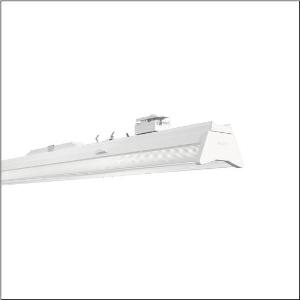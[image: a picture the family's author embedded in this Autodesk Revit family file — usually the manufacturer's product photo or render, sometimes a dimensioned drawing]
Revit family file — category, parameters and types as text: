
# Revit family: licross_r__21_performance_mo_52td16dn46xg_ca4f
name_source: partatom
category: Lighting Fixtures
units: mm (PartAtom-declared; Revit-internal decimal feet)

## family parameters
Cut with Voids When Loaded = No
Host = Face
Light Source = No
Part Type = Normal
Room Calculation Point = No
Round Connector Dimension = Use Diameter
Shared = No

## types (1)
- --- (1 x LED, 6000 lm, 32.7 W, 4000K)
    Apparent Load = 33 VA
    CIE Flux Codes = 66 88 96 79 100
    Color Rendering = 80
    Color Temperature = 4000K
    Default Elevation = 1800 mm
    Description = Licross® 21 Performance MO, luminaire insert, of sheet steel, galvanised, coil coated, white, length: 1.500mm, width: 120mm, height: 123mm, LED rated luminous flux: 6.000lm, light colour: 840, control gear: DALI 2, with plug, 5-pole, with phase selection, mains connection: 220..240V, AC, 50/60Hz, rated input power: 33W, halogen-free wiring, primary light control with lens, of plastic, primary optical cover: cover, of PMMA, light emission: direct/indirect distribution, primary light characteristic: symmetric, protection rating (complete): IP54, insulation class (complete): insulation class I (protective earthing), certification: CE, ENEC, VDE, UKCA, protection symbol: D if used in an environment with non-conductive dust loads with corresponding accessories, impact resistance: IK06, permissible ambient temperature for indoor applications: -25..+45°C, corresponds to IFS (International Featured Standards) requirements for safety and quality in the food industry, reducing of maximum allowable ambient temperature of 5°C with ceiling mounting, LABS conformity tested according to VDMA 24364:2018-05, packaging unit: 1 piece
    Height = 114 mm
    Lamp = 1 x LED
    Lamp Light Flux = 6000 lm
    Lamp Power = 32.7 W
    Lamp count = 1
    Length = 1500 mm
    Luminous efficacy = 183 lm/W
    Manufacturer = Siteco
    ModVariant = No
    Model = 52TD16DN46XG
    Mounting Place = Ceiling
    Mounting Type = Pendant
    Number of Poles = 1
    OnlyDefault = Yes
    Power Factor = 1
    Product Name = Licross® 21 Performance MO
    Product group = luminaire insert
    ProductGroupID = 901
    Protection Class = Protection class I
    Protection Degree = IP 54
    RLX_Detail_Level = 1
    RLX_Emergency_Light_Flux = 0 lm
    RLX_Emergency_Type = 0
    RLX_Emergency_Type_DB = No
    RlxData = <blob elided: 33645 chars, md5=c97371f8>
    Socket = socket
    Standby Power = 0 W
    System Light Flux = 6000 lm
    System Power = 33 W
    Type Comments = factory setting: luminous flux: 100 % | dim-lin: 254 | 222 mA
    Type Image = l_1256138.jpg
    URL = http://relux.com
    VarID = @adj_099531
    Voltage = 0 V
    Weight = 0.00 kg
    Width = 120 mm

## geometry (parser evidence)
native form markers: Blend x4, Sweep x13
no freeform markers — native parametric forms only
